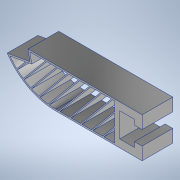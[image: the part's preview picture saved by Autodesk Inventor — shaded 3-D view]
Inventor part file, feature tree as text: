
AUTODESK INVENTOR PART (.ipt)
format: ipt  version: 2022 (Build 260153000, 153)  size: 309,248 bytes
history: native  units: mm
features: extrude x6, sketch x4, fillet x1, shell x1, projected_geometry x1
ambient origin geometry x8: Origin, YZ Plane, XZ Plane, XY Plane, X Axis, Y Axis, Z Axis, Center Point
bodies: Body1 (feature_tree)
feature tree (13):
  extrude  "Extrusion2"  Depth=44.0mm
  extrude  "Extrusion5"  Depth=12.0mm TaperAngle=0.0deg
  fillet  "Fillet2"  Radius=45.0mm
  shell  "Shell1"  Thickness=15.6mm
  extrude  "Extrusion7"  TaperAngle=0.0deg  [1 undecoded]
  extrude  "Extrusion8"  Depth=9.6mm
  extrude  "Extrusion9"  Depth=12.0mm
  extrude  "Extrusion10"  Depth=12.0mm
  sketch  "Sketch8"  dims[d41=5.8mm d48=44.0mm]
  sketch  "Sketch13"  dims[d50=3.0mm d56=12.0mm d57=0.0mm d63=45.0mm d67=15.6mm d71=0.0mm]
  sketch  "Sketch14"  dims[d80=17.453293mm d82=0.0mm d83=0.0mm]
  projected_geometry  "Projected Loop1"
  sketch  "Sketch16"  dims[d87=5.6mm d88=9.6mm d95=4.0mm d96=9.0mm d97=15.6mm d98=23.0mm d99=0.62mm d100=12.0mm d101=0.0mm d102=10.747401mm d103=12.0mm d104=0.0mm d105=0.38mm d1=0.38mm d127=12.0mm d128=0.0mm d130=22.68928mm d132=22.68928mm d133=0.38mm d135=0.38mm d136=0.38mm d137=0.38mm d138=0.38mm d139=0.38mm d140=0.38mm d141=0.38mm d143=0.38mm d152=22.68928mm d153=12.0mm d154=0.0mm d155=4.3mm d156=4.3mm d157=4.3mm d158=4.3mm d159=4.3mm d160=4.3mm d161=4.3mm d162=4.3mm d164=4.3mm]
note: 1 required parameter value undecoded (feature->parameter linkage not recoverable at this tier; creation-order binding heuristic only, values carry confidence <= 0.55)
